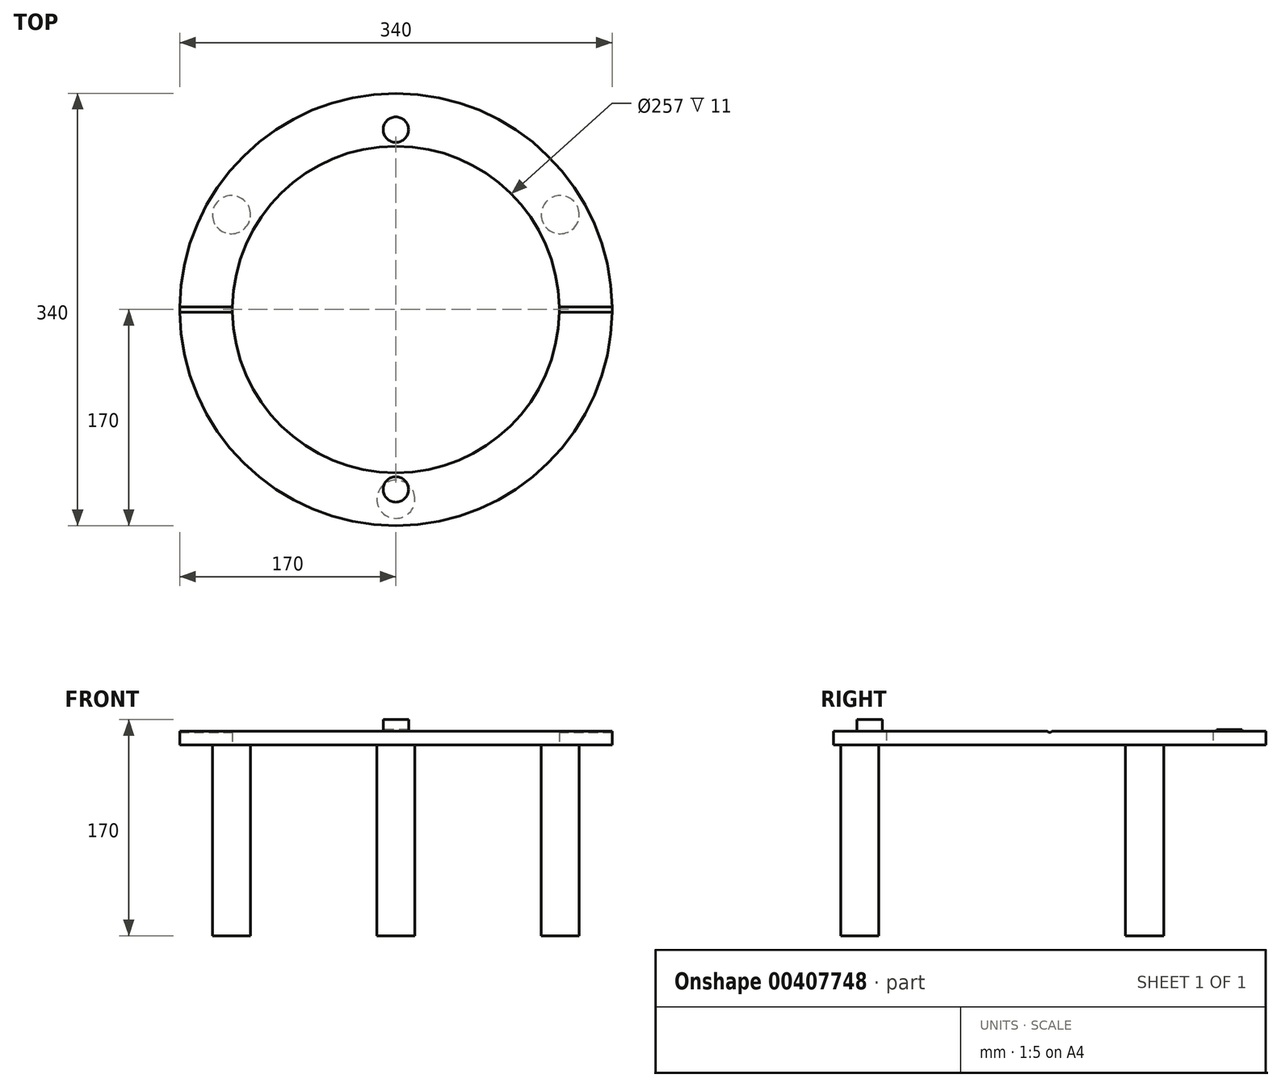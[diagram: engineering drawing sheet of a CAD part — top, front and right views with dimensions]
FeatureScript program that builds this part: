
annotation { "Feature Type Name" : "Feature", "Feature Type Description" : "" }
export const myFeature = defineFeature(function(context is Context, id is Id, definition is map)
    precondition{}
    {
        {
            var Q0;
            Q0=qCreatedBy(makeId("Top.planeOp"),FACE);
            var sketch = newSketch(context, id + "F0", { "sketchPlane" : qUnion([Q0])});
            skCircle(sketch, "E0", {"center": v(0, 0) * mm, "radius": 128.5 * mm});
            skCircle(sketch, "E1", {"center": v(0, 0) * mm, "radius": 170 * mm});
            skSolve(sketch);
        }
        {
            var Q0;
            Q0=makeQuery(id+"F0.imprint","IMPRINT",FACE,{"disambiguationData":[TD([[makeQuery(id+"F0.imprint","IMPRINT",EDGE,{"derivedFrom":sQuery(id+"F0.wireOp",EDGE,"E0")}),-1.0]])]});
            extrude(context, id + "F1", {"entities" : qUnion([Q0]), "depth" : 7.5 * mm, "offsetDistance" : 25 * mm});
        }
        {
            var Q0;
            Q0=makeQuery(id+"F1.opExtrude","CAP_FACE",FACE,{"disambiguationData":[OSD([sQuery(id+"F0.wireOp",EDGE,"E0"),sQuery(id+"F0.wireOp",EDGE,"E1")])],"isStart":true});
            extrude(context, id + "F2", {"entities" : qUnion([Q0]), "operationType" : NewBodyOperationType.ADD, "depth" : 12.5 * mm, "offsetDistance" : 25 * mm});
        }
        {
            var Q0;
            Q0=makeQuery(id+"F2.opExtrude","CAP_FACE",FACE,{"disambiguationData":[OSD([sQuery(id+"F0.wireOp",EDGE,"E0"),sQuery(id+"F0.wireOp",EDGE,"E1")])],"isStart":false});
            var sketch = newSketch(context, id + "F3", { "sketchPlane" : qUnion([Q0])});
            skCircle(sketch, "E2", {"center": v(0, 149.25) * mm, "radius": 15 * mm});
            skCircle(sketch, "E3.1.0", {"center": v(129.25, -74.62) * mm, "radius": 15 * mm});
            skCircle(sketch, "E3.2.0", {"center": v(-129.25, -74.63) * mm, "radius": 15 * mm});
            skPoint(sketch, "E3.center", {"position": v(0, 0) * mm});
            skLineSegment(sketch, "E3.anchor1", {"start": v(0, 0) * mm, "end": v(0, 149.25) * mm, "construction": true});
            skLineSegment(sketch, "E3.anchor2", {"start": v(0, 0) * mm, "end": v(-129.25, -74.63) * mm, "construction": true});
            skSolve(sketch);
        }
        {
            var Q0;
            Q0=qSketchRegion(id+"F3",true);
            extrude(context, id + "F4", {"entities" : qUnion([Q0]), "operationType" : NewBodyOperationType.ADD, "depth" : 150 * mm, "offsetDistance" : 25 * mm});
        }
        {
            var Q0;
            Q0=makeQuery(id+"F1.opExtrude","CAP_FACE",FACE,{"disambiguationData":[OSD([sQuery(id+"F0.wireOp",EDGE,"E0"),sQuery(id+"F0.wireOp",EDGE,"E1")])],"isStart":false});
            var sketch = newSketch(context, id + "F5", { "sketchPlane" : qUnion([Q0])});
            skCircle(sketch, "E4", {"center": v(0, 141.5) * mm, "radius": 10 * mm});
            skCircle(sketch, "E5.MirrorC", {"center": v(0, -141.5) * mm, "radius": 10 * mm});
            skSolve(sketch);
        }
        {
            var Q0;
            Q0=makeQuery(id+"F5.imprint","IMPRINT",FACE,{"disambiguationData":[TD([[makeQuery(id+"F5.imprint","IMPRINT",EDGE,{"derivedFrom":sQuery(id+"F5.wireOp",EDGE,"E4")}),1.0]])]});
            extrude(context, id + "F6", {"entities" : qUnion([Q0]), "operationType" : NewBodyOperationType.REMOVE, "oppositeDirection" : true, "depth" : 8 * mm, "offsetDistance" : 25 * mm});
        }
        {
            var Q0;
            Q0=makeQuery(id+"F5.imprint","IMPRINT",FACE,{"disambiguationData":[TD([[makeQuery(id+"F5.imprint","IMPRINT",EDGE,{"derivedFrom":sQuery(id+"F5.wireOp",EDGE,"E5.MirrorC")}),-1.0]])]});
            extrude(context, id + "F7", {"entities" : qUnion([Q0]), "operationType" : NewBodyOperationType.REMOVE, "oppositeDirection" : true, "depth" : 9 * mm, "offsetDistance" : 25 * mm});
        }
        {
            var Q0;
            Q0=qCreatedBy(makeId("Top.planeOp"),FACE);
            var sketch = newSketch(context, id + "F8", { "sketchPlane" : qUnion([Q0])});
            skCircle(sketch, "E6.0.0", {"center": v(0, 0) * mm, "radius": 128.5 * mm, "construction": true});
            skCircle(sketch, "E7.0", {"center": v(0, 0) * mm, "radius": 170 * mm, "construction": true});
            skLineSegment(sketch, "E8", {"start": v(0, 86.47) * mm, "end": v(0, -74.04) * mm, "construction": true});
            skLineSegment(sketch, "E9", {"start": v(-70.64, 0) * mm, "end": v(92.25, 0) * mm, "construction": true});
            skLineSegment(sketch, "E10", {"start": v(-236.07, 0) * mm, "end": v(279.16, 0) * mm});
            skLineSegment(sketch, "E11", {"start": v(279.16, 0) * mm, "end": v(279.16, 2.5) * mm});
            skLineSegment(sketch, "E12", {"start": v(279.16, 2.5) * mm, "end": v(-236.07, 2.5) * mm});
            skLineSegment(sketch, "E13", {"start": v(-236.07, 2.5) * mm, "end": v(-236.07, 0) * mm});
            skSolve(sketch);
        }
        {
            var Q0;
            Q0=makeQuery(id+"F8.imprint","IMPRINT",FACE,{"disambiguationData":[TD([[makeQuery(id+"F8.imprint","IMPRINT",EDGE,{"derivedFrom":sQuery(id+"F8.wireOp",EDGE,"E10")}),1.0]])]});
            var Q1;
            Q1=sQuery(id+"F8.wireOp",EDGE,"E10");
            revolve(context, id + "F9", {"operationType" : NewBodyOperationType.REMOVE, "surfaceOperationType" : NewSurfaceOperationType.NEW, "entities" : qUnion([Q0]), "axis" : qUnion([Q1]), "revolveType" : RevolveType.FULL, "oppositeDirection" : true});
        }
    });
